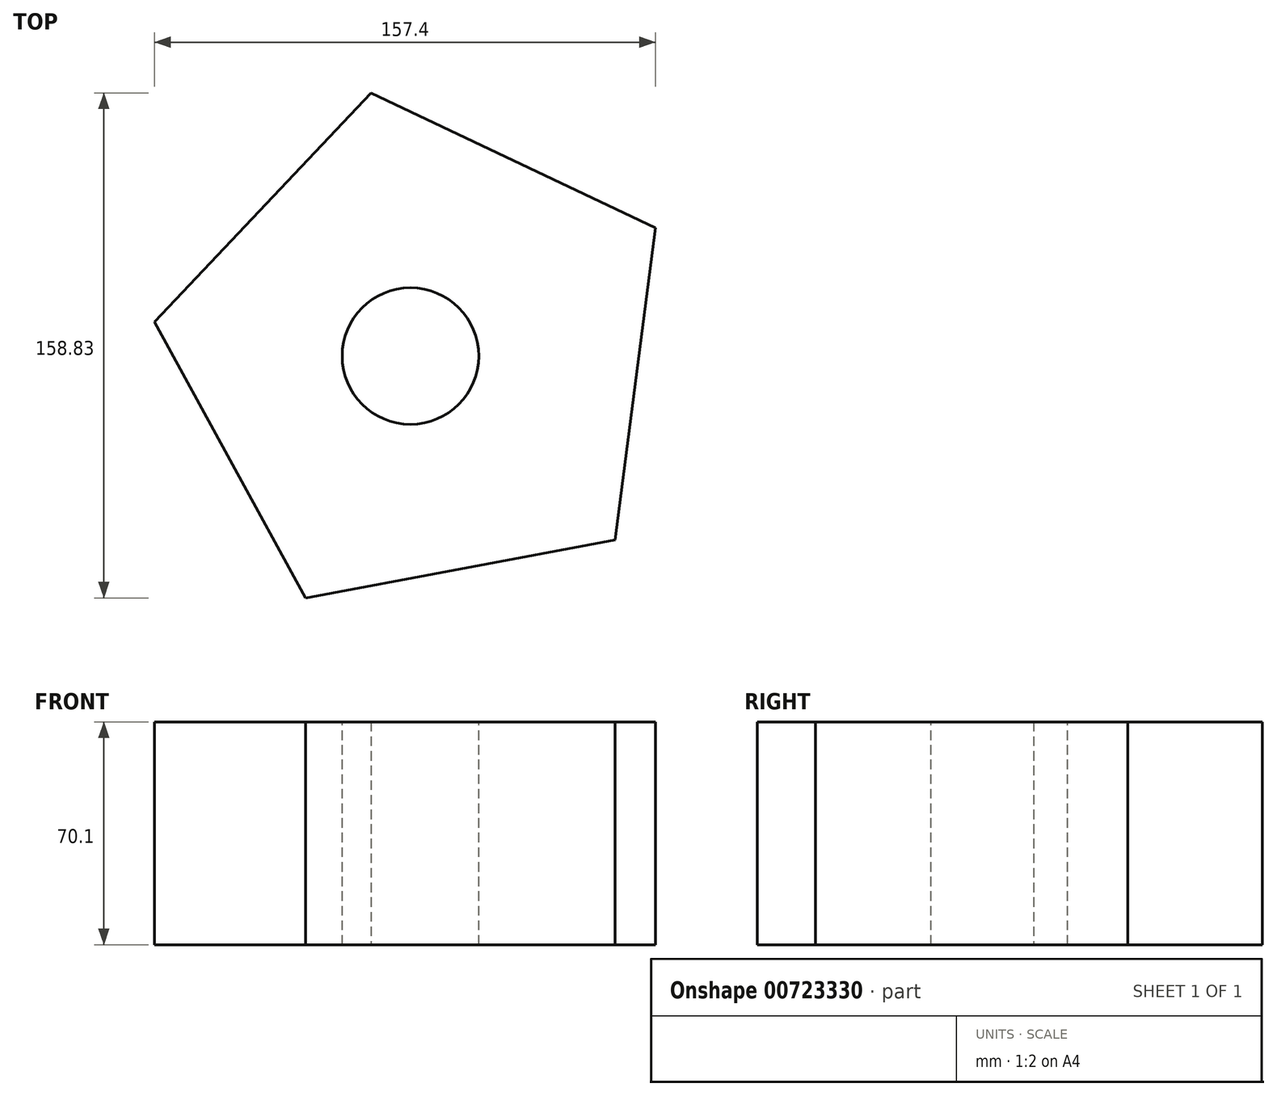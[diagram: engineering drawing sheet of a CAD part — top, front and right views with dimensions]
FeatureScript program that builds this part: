
annotation { "Feature Type Name" : "Feature", "Feature Type Description" : "" }
export const myFeature = defineFeature(function(context is Context, id is Id, definition is map)
    precondition{}
    {
        {
            var Q0;
            Q0=qCreatedBy(makeId("Top.planeOp"),FACE);
            var sketch = newSketch(context, id + "F0", { "sketchPlane" : qUnion([Q0])});
            skCircle(sketch, "E0.cCircle", {"center": v(0, 0) * mm, "radius": 68.12 * mm, "construction": true});
            skLineSegment(sketch, "E0.0", {"start": v(-36.07, -76.08) * mm, "end": v(-83.5, 10.8) * mm});
            skLineSegment(sketch, "E0.1", {"start": v(-83.5, 10.8) * mm, "end": v(-15.54, 82.75) * mm});
            skLineSegment(sketch, "E0.2", {"start": v(-15.54, 82.75) * mm, "end": v(73.9, 40.35) * mm});
            skLineSegment(sketch, "E0.3", {"start": v(73.9, 40.35) * mm, "end": v(61.21, -57.81) * mm});
            skLineSegment(sketch, "E0.4", {"start": v(61.21, -57.81) * mm, "end": v(-36.07, -76.08) * mm});
            skPoint(sketch, "E0.0.midPoint", {"position": v(-59.79, -32.65) * mm});
            skSolve(sketch);
        }
        {
            var Q0;
            Q0=makeQuery(id+"F0.imprint","IMPRINT",FACE,{"disambiguationData":[TD([[makeQuery(id+"F0.imprint","IMPRINT",EDGE,{"derivedFrom":sQuery(id+"F0.wireOp",EDGE,"E0.0")}),-1.0]])]});
            extrude(context, id + "F1", {"entities" : qUnion([Q0]), "depth" : 70.1 * mm, "offsetDistance" : 25.4 * mm});
        }
        {
            var Q0;
            Q0=makeQuery(id+"F1.opExtrude","CAP_FACE",FACE,{"disambiguationData":[OSD([sQuery(id+"F0.wireOp",EDGE,"E0.0"),sQuery(id+"F0.wireOp",EDGE,"E0.1"),sQuery(id+"F0.wireOp",EDGE,"E0.2"),sQuery(id+"F0.wireOp",EDGE,"E0.3"),sQuery(id+"F0.wireOp",EDGE,"E0.4")])],"isStart":false});
            var sketch = newSketch(context, id + "F2", { "sketchPlane" : qUnion([Q0])});
            skCircle(sketch, "E1", {"center": v(-3.1, 0) * mm, "radius": 21.47 * mm});
            skSolve(sketch);
        }
        {
            var Q0;
            Q0=makeQuery(id+"F2.imprint","IMPRINT",FACE,{"disambiguationData":[TD([[makeQuery(id+"F2.imprint","IMPRINT",EDGE,{"derivedFrom":sQuery(id+"F2.wireOp",EDGE,"E1")}),1.0]])]});
            extrude(context, id + "F3", {"entities" : qUnion([Q0]), "operationType" : NewBodyOperationType.REMOVE, "oppositeDirection" : true, "depth" : 109.47 * mm, "offsetDistance" : 25.4 * mm});
        }
    });
